# Revit family: RC + 280 types Avec hôte
name_source: partatom
category: Dispositifs d'éclairage
units: mm (PartAtom-declared; Revit-internal decimal feet)

## family parameters
Conserver l'orientation des annotations = Oui
Cote de connecteur circulaire = Utiliser le diamètre
Couper avec des vides une fois chargée = Non
Hôte = Face
Partagée = Non
Point de calcul de pièce = Non
Type d'élément = Normal

## types (2) — shared parameters
Alimentation = 110-240 V AC
Classe = II
Code d'assemblage = D5010200
Elévation par défaut = 250 cm
Fabricant = B.E.G.
Hauteur de montage max = 400 cm
IP = 54
Image du type = MURAL.jpg
Marque = LUXOMAT
Mode de pose = Mural
Position en hauteur = 250 cm
Température ambiante = -25°C à +50°C
URL = http://www.luxomat.com

## per-type parameters (varying)
| type | Charge Cos ɸ =0.5 | Charge Cos ɸ =1 | Charge LED | Commentaires du type | Consommation | Modèle | Relais | Référence | Type de Sortie |
| 01- RC + 280 Générique |  |  |  | DET.MOUV.130°/20M MURAL |  | RC + 280 |  |  |  |
| 02- RC + next N 280 réf 93341 | 1500 VA | 3000 W | 300 W | DET.MOUV.1 CONTACT.130°/20M MURAL | 0,5 W | RC + N 280 | 16 A | 93341 | TOR |

## geometry (parser evidence)
native form markers: Extrusion x1
no freeform markers — native parametric forms only
